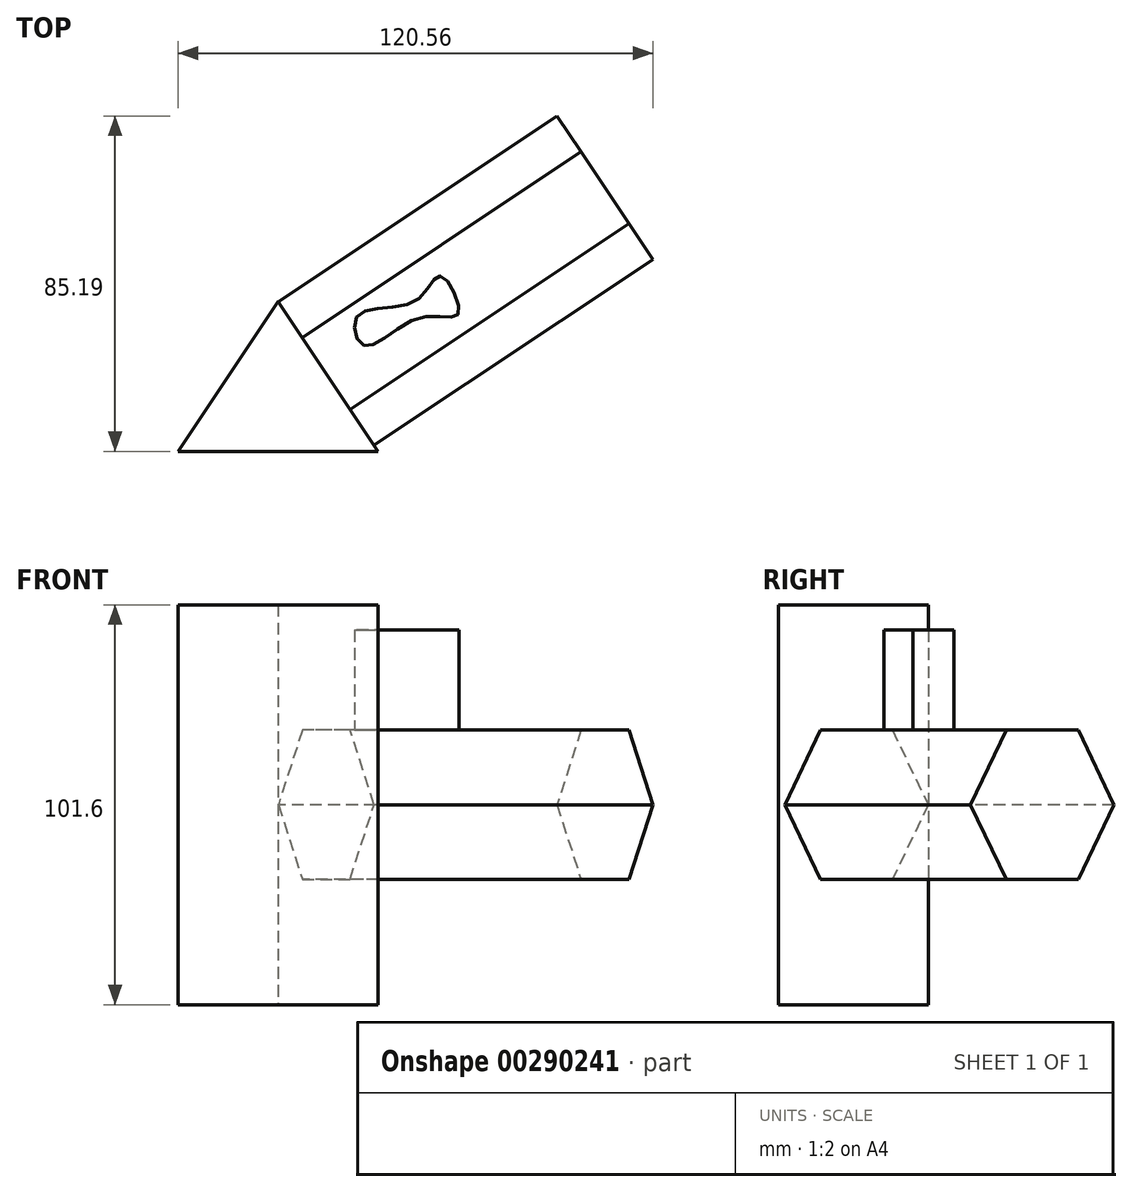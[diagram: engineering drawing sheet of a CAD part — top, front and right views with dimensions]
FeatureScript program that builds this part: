
annotation { "Feature Type Name" : "Feature", "Feature Type Description" : "" }
export const myFeature = defineFeature(function(context is Context, id is Id, definition is map)
    precondition{}
    {
        {
            var Q0;
            Q0=qCreatedBy(makeId("Top.planeOp"),FACE);
            var sketch = newSketch(context, id + "F0", { "sketchPlane" : qUnion([Q0])});
            skLineSegment(sketch, "E0", {"start": v(0, 0) * mm, "end": v(-25.4, -38.1) * mm});
            skLineSegment(sketch, "E1", {"start": v(-25.4, -38.1) * mm, "end": v(25.4, -38.1) * mm});
            skLineSegment(sketch, "E2", {"start": v(25.4, -38.1) * mm, "end": v(0, 0) * mm});
            skSolve(sketch);
        }
        {
            var Q0;
            Q0 = qSketchRegion(id + "F0", true);
            extrude(context, id + "F1", {"entities" : qUnion([Q0]), "endBound" : BoundingType.SYMMETRIC, "depth" : 101.6 * mm});
        }
        {
            var Q0;
            Q0=makeQuery(id+"F1.opExtrude","SWEPT_FACE",FACE,{"disambiguationData":[OSD([sQuery(id+"F0.wireOp",EDGE,"E2")])]});
            var sketch = newSketch(context, id + "F2", { "sketchPlane" : qUnion([Q0])});
            skCircle(sketch, "E3.cCircle", {"center": v(-22.02, 0) * mm, "radius": 18.96 * mm, "construction": true});
            skLineSegment(sketch, "E3.0", {"start": v(-32.97, 18.96) * mm, "end": v(-11.08, 18.96) * mm});
            skLineSegment(sketch, "E3.1", {"start": v(-11.08, 18.96) * mm, "end": v(-0.13, 0) * mm});
            skLineSegment(sketch, "E3.2", {"start": v(-0.13, 0) * mm, "end": v(-11.08, -18.96) * mm});
            skLineSegment(sketch, "E3.3", {"start": v(-11.08, -18.96) * mm, "end": v(-32.97, -18.96) * mm});
            skLineSegment(sketch, "E3.4", {"start": v(-32.97, -18.96) * mm, "end": v(-43.92, 0) * mm});
            skLineSegment(sketch, "E3.5", {"start": v(-43.92, 0) * mm, "end": v(-32.97, 18.96) * mm});
            skPoint(sketch, "E3.0.midPoint", {"position": v(-22.02, 18.96) * mm});
            skSolve(sketch);
        }
        {
            var Q0;
            Q0=makeQuery(id+"F2.imprint","IMPRINT",FACE,{"disambiguationData":[TD([[makeQuery(id+"F2.imprint","IMPRINT",EDGE,{"derivedFrom":sQuery(id+"F2.wireOp",EDGE,"E3.0")}),-1.0]])]});
            extrude(context, id + "F3", {"entities" : qUnion([Q0]), "operationType" : NewBodyOperationType.ADD, "depth" : 85.1 * mm});
        }
        {
            var Q0;
            Q0=makeQuery(id+"F3.opExtrude","SWEPT_FACE",FACE,{"disambiguationData":[OSD([sQuery(id+"F2.wireOp",EDGE,"E3.0")])]});
            var sketch = newSketch(context, id + "F4", { "sketchPlane" : qUnion([Q0])});
            skFitSpline(sketch, "E4", {"points": [v(21.79, -11.17) * mm, v(35.91, -4.2) * mm, v(45.78, -3.05) * mm, v(41.33, 6.44) * mm, v(34.75, 0) * mm, v(20.24, -3.63) * mm, v(21.79, -11.17) * mm]});
            skSolve(sketch);
        }
        {
            var Q0;
            Q0=makeQuery(id+"F4.imprint","IMPRINT",FACE,{"disambiguationData":[TD([[makeQuery(id+"F4.imprint","IMPRINT",EDGE,{"derivedFrom":sQuery(id+"F4.wireOp",EDGE,"E4")}),1.0]])]});
            extrude(context, id + "F5", {"entities" : qUnion([Q0]), "operationType" : NewBodyOperationType.ADD, "depth" : 25.4 * mm});
        }
    });
